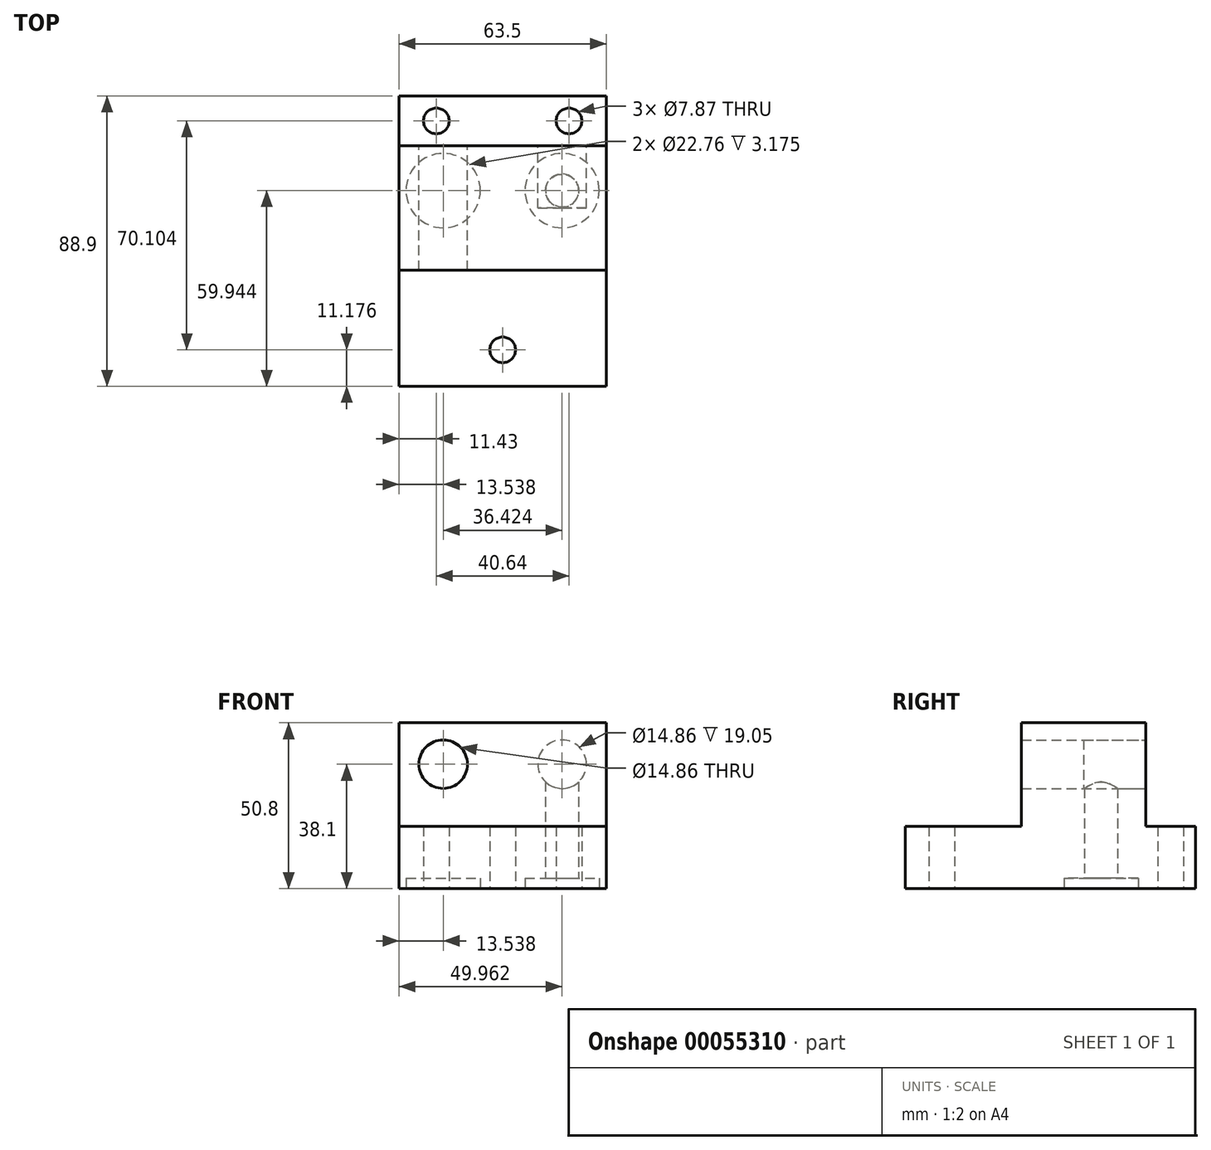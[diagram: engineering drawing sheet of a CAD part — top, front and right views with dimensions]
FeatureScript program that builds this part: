
annotation { "Feature Type Name" : "Feature", "Feature Type Description" : "" }
export const myFeature = defineFeature(function(context is Context, id is Id, definition is map)
    precondition{}
    {
        {
            var Q0;
            Q0=qCreatedBy(makeId("Top.planeOp"),FACE);
            var sketch = newSketch(context, id + "F0", { "sketchPlane" : qUnion([Q0])});
            skLineSegment(sketch, "E0.bottom", {"start": v(0, 0) * mm, "end": v(63.5, 0) * mm});
            skLineSegment(sketch, "E0.top", {"start": v(0, 88.9) * mm, "end": v(63.5, 88.9) * mm});
            skLineSegment(sketch, "E0.left", {"start": v(0, 0) * mm, "end": v(0, 88.9) * mm});
            skLineSegment(sketch, "E0.right", {"start": v(63.5, 0) * mm, "end": v(63.5, 88.9) * mm});
            skCircle(sketch, "E1", {"center": v(11.43, 81.28) * mm, "radius": 3.94 * mm});
            skCircle(sketch, "E2", {"center": v(52.07, 81.28) * mm, "radius": 3.94 * mm});
            skCircle(sketch, "E3", {"center": v(31.75, 11.18) * mm, "radius": 3.94 * mm});
            skCircle(sketch, "E4", {"center": v(13.54, 59.94) * mm, "radius": 7.43 * mm});
            skCircle(sketch, "E5", {"center": v(49.96, 59.94) * mm, "radius": 7.43 * mm});
            skLineSegment(sketch, "E6.bottom", {"start": v(0, 73.66) * mm, "end": v(63.5, 73.66) * mm});
            skLineSegment(sketch, "E6.top", {"start": v(0, 35.56) * mm, "end": v(63.5, 35.56) * mm});
            skLineSegment(sketch, "E6.left", {"start": v(0, 73.66) * mm, "end": v(0, 35.56) * mm});
            skLineSegment(sketch, "E6.right", {"start": v(63.5, 73.66) * mm, "end": v(63.5, 35.56) * mm});
            skSolve(sketch);
        }
        {
            var Q0;
            {var subQ1=sQuery(id+"F0.wireOp",EDGE,"E0.top");Q0=makeQuery(id+"F0.imprint","IMPRINT",FACE,{"disambiguationData":[TD([[makeQuery(id+"F0.imprint","IMPRINT",EDGE,{"derivedFrom":subQ1}),-1.0]])]});}
            var Q1;
            Q1=makeQuery(id+"F0.imprint","IMPRINT",FACE,{"disambiguationData":[TD([[makeQuery(id+"F0.imprint","IMPRINT",EDGE,{"derivedFrom":sQuery(id+"F0.wireOp",EDGE,"E4")}),-1.0]])]});
            var Q2;
            Q2=makeQuery(id+"F0.imprint","IMPRINT",FACE,{"disambiguationData":[TD([[makeQuery(id+"F0.imprint","IMPRINT",EDGE,{"derivedFrom":sQuery(id+"F0.wireOp",EDGE,"E4")}),1.0]])]});
            var Q3;
            Q3=makeQuery(id+"F0.imprint","IMPRINT",FACE,{"disambiguationData":[TD([[makeQuery(id+"F0.imprint","IMPRINT",EDGE,{"derivedFrom":sQuery(id+"F0.wireOp",EDGE,"E5")}),1.0]])]});
            var Q4;
            {var subQ1=sQuery(id+"F0.wireOp",EDGE,"E0.bottom");Q4=makeQuery(id+"F0.imprint","IMPRINT",FACE,{"disambiguationData":[TD([[makeQuery(id+"F0.imprint","IMPRINT",EDGE,{"derivedFrom":subQ1}),1.0]])]});}
            extrude(context, id + "F1", {"entities" : qUnion([Q0, Q1, Q2, Q3, Q4]), "depth" : 19.05 * mm});
        }
        {
            var Q0;
            Q0=makeQuery(id+"F1.opExtrude","CAP_FACE",FACE,{"disambiguationData":[OSD([sQuery(id+"F0.wireOp",EDGE,"E0.bottom"),sQuery(id+"F0.wireOp",EDGE,"E0.top"),sQuery(id+"F0.wireOp",EDGE,"E0.left"),sQuery(id+"F0.wireOp",EDGE,"E0.right"),sQuery(id+"F0.wireOp",EDGE,"E1"),sQuery(id+"F0.wireOp",EDGE,"E2"),sQuery(id+"F0.wireOp",EDGE,"E3"),sQuery(id+"F0.wireOp",EDGE,"E4"),sQuery(id+"F0.wireOp",EDGE,"E5")])],"isStart":true});
            var sketch = newSketch(context, id + "F2", { "sketchPlane" : qUnion([Q0])});
            skCircle(sketch, "E7", {"center": v(49.96, -59.94) * mm, "radius": 11.38 * mm});
            skCircle(sketch, "E8", {"center": v(13.54, -59.94) * mm, "radius": 11.38 * mm});
            skSolve(sketch);
        }
        {
            var Q0;
            Q0=makeQuery(id+"F1.opExtrude","SWEPT_BODY",BODY,{"disambiguationData":[OSD([sQuery(id+"F0.wireOp",EDGE,"E0.bottom"),sQuery(id+"F0.wireOp",EDGE,"E0.top"),sQuery(id+"F0.wireOp",EDGE,"E0.left"),sQuery(id+"F0.wireOp",EDGE,"E0.right"),sQuery(id+"F0.wireOp",EDGE,"E1"),sQuery(id+"F0.wireOp",EDGE,"E2"),sQuery(id+"F0.wireOp",EDGE,"E3"),sQuery(id+"F0.wireOp",EDGE,"E4"),sQuery(id+"F0.wireOp",EDGE,"E5")])]});
            transform(context, id + "F3", {"entities" : qUnion([Q0]), "transformType" : TransformType.TRANSLATION_3D, "dx" : -152.4 * mm, "dy" : 0 * mm, "dz" : 0 * mm, "makeCopy" : true});
        }
        {
            var Q0;
            Q0=makeQuery(id+"F3.opPattern","COPY",BODY,{"derivedFrom":makeQuery(id+"F1.opExtrude","SWEPT_BODY",BODY,{"disambiguationData":[OSD([sQuery(id+"F0.wireOp",EDGE,"E0.bottom"),sQuery(id+"F0.wireOp",EDGE,"E0.top"),sQuery(id+"F0.wireOp",EDGE,"E0.left"),sQuery(id+"F0.wireOp",EDGE,"E0.right"),sQuery(id+"F0.wireOp",EDGE,"E1"),sQuery(id+"F0.wireOp",EDGE,"E2"),sQuery(id+"F0.wireOp",EDGE,"E3"),sQuery(id+"F0.wireOp",EDGE,"E4"),sQuery(id+"F0.wireOp",EDGE,"E5")])]}),"instanceName":"1"});
            deleteBodies(context, id + "F4", {"entities" : qUnion([Q0])});
        }
        {
            var Q0;
            Q0=makeQuery(id+"F0.imprint","IMPRINT",FACE,{"disambiguationData":[TD([[makeQuery(id+"F0.imprint","IMPRINT",EDGE,{"derivedFrom":sQuery(id+"F0.wireOp",EDGE,"E5")}),1.0]])]});
            var Q1;
            Q1=makeQuery(id+"F0.imprint","IMPRINT",FACE,{"disambiguationData":[TD([[makeQuery(id+"F0.imprint","IMPRINT",EDGE,{"derivedFrom":sQuery(id+"F0.wireOp",EDGE,"E4")}),1.0]])]});
            var Q2;
            Q2=makeQuery(id+"F0.imprint","IMPRINT",FACE,{"disambiguationData":[TD([[makeQuery(id+"F0.imprint","IMPRINT",EDGE,{"derivedFrom":sQuery(id+"F0.wireOp",EDGE,"E4")}),-1.0]])]});
            extrude(context, id + "F5", {"entities" : qUnion([Q0, Q1, Q2]), "operationType" : NewBodyOperationType.ADD, "depth" : 50.8 * mm});
        }
        {
            var Q0;
            Q0=makeQuery(id+"F5.opExtrude","SWEPT_FACE",FACE,{"disambiguationData":[OSD([sQuery(id+"F0.wireOp",EDGE,"E6.bottom")])]});
            var sketch = newSketch(context, id + "F6", { "sketchPlane" : qUnion([Q0])});
            skCircle(sketch, "E9", {"center": v(-49.96, 38.1) * mm, "radius": 7.43 * mm});
            skCircle(sketch, "E10", {"center": v(-13.54, 38.1) * mm, "radius": 7.43 * mm});
            skSolve(sketch);
        }
        {
            var Q0;
            Q0=makeQuery(id+"F0.imprint","IMPRINT",FACE,{"disambiguationData":[TD([[makeQuery(id+"F0.imprint","IMPRINT",EDGE,{"derivedFrom":sQuery(id+"F0.wireOp",EDGE,"E5")}),1.0]])]});
            var Q1;
            Q1=makeQuery(id+"F0.imprint","IMPRINT",FACE,{"disambiguationData":[TD([[makeQuery(id+"F0.imprint","IMPRINT",EDGE,{"derivedFrom":sQuery(id+"F0.wireOp",EDGE,"E4")}),1.0]])]});
            extrude(context, id + "F7", {"entities" : qUnion([Q0, Q1]), "operationType" : NewBodyOperationType.REMOVE, "depth" : 3.17 * mm});
        }
        {
            var Q0;
            Q0=makeQuery(id+"F7.boolean.opBoolean","COPY",FACE,{"derivedFrom":makeQuery(id+"F7.opExtrude","CAP_FACE",FACE,{"disambiguationData":[OSD([sQuery(id+"F0.wireOp",EDGE,"E5")])],"isStart":false})});
            var sketch = newSketch(context, id + "F8", { "sketchPlane" : qUnion([Q0])});
            skCircle(sketch, "E11", {"center": v(49.96, -59.94) * mm, "radius": 5.08 * mm});
            skCircle(sketch, "E12", {"center": v(13.54, -59.94) * mm, "radius": 5.08 * mm});
            skSolve(sketch);
        }
        {
            var Q0;
            Q0=makeQuery(id+"F2.imprint","IMPRINT",FACE,{"disambiguationData":[TD([[makeQuery(id+"F2.imprint","IMPRINT",EDGE,{"derivedFrom":sQuery(id+"F2.wireOp",EDGE,"E7")}),1.0]])]});
            var Q1;
            Q1=makeQuery(id+"F2.imprint","IMPRINT",FACE,{"disambiguationData":[TD([[makeQuery(id+"F2.imprint","IMPRINT",EDGE,{"derivedFrom":sQuery(id+"F2.wireOp",EDGE,"E8")}),1.0]])]});
            extrude(context, id + "F9", {"entities" : qUnion([Q0, Q1]), "operationType" : NewBodyOperationType.REMOVE, "oppositeDirection" : true, "depth" : 3.17 * mm});
        }
        {
            var Q0;
            Q0=makeQuery(id+"F6.imprint","IMPRINT",FACE,{"disambiguationData":[TD([[makeQuery(id+"F6.imprint","IMPRINT",EDGE,{"derivedFrom":sQuery(id+"F6.wireOp",EDGE,"E9")}),1.0]])]});
            extrude(context, id + "F10", {"entities" : qUnion([Q0]), "operationType" : NewBodyOperationType.REMOVE, "oppositeDirection" : true, "depth" : 19.05 * mm});
        }
        {
            var Q0;
            Q0=makeQuery(id+"F6.imprint","IMPRINT",FACE,{"disambiguationData":[TD([[makeQuery(id+"F6.imprint","IMPRINT",EDGE,{"derivedFrom":sQuery(id+"F6.wireOp",EDGE,"E10")}),1.0]])]});
            extrude(context, id + "F11", {"entities" : qUnion([Q0]), "operationType" : NewBodyOperationType.REMOVE, "endBound" : BoundingType.THROUGH_ALL, "oppositeDirection" : true, "depth" : 25.4 * mm});
        }
        {
            var Q0;
            Q0=makeQuery(id+"F8.imprint","IMPRINT",FACE,{"disambiguationData":[TD([[makeQuery(id+"F8.imprint","IMPRINT",EDGE,{"derivedFrom":sQuery(id+"F8.wireOp",EDGE,"47ca692f-d630-4584-b53f-369725f0df87")}),1.0]])]});
            var Q1;
            Q1=makeQuery(id+"F8.imprint","IMPRINT",FACE,{"disambiguationData":[TD([[makeQuery(id+"F8.imprint","IMPRINT",EDGE,{"derivedFrom":sQuery(id+"F8.wireOp",EDGE,"E11")}),1.0]])]});
            extrude(context, id + "F12", {"entities" : qUnion([Q0, Q1]), "operationType" : NewBodyOperationType.REMOVE, "oppositeDirection" : true, "depth" : 31.75 * mm});
        }
    });
